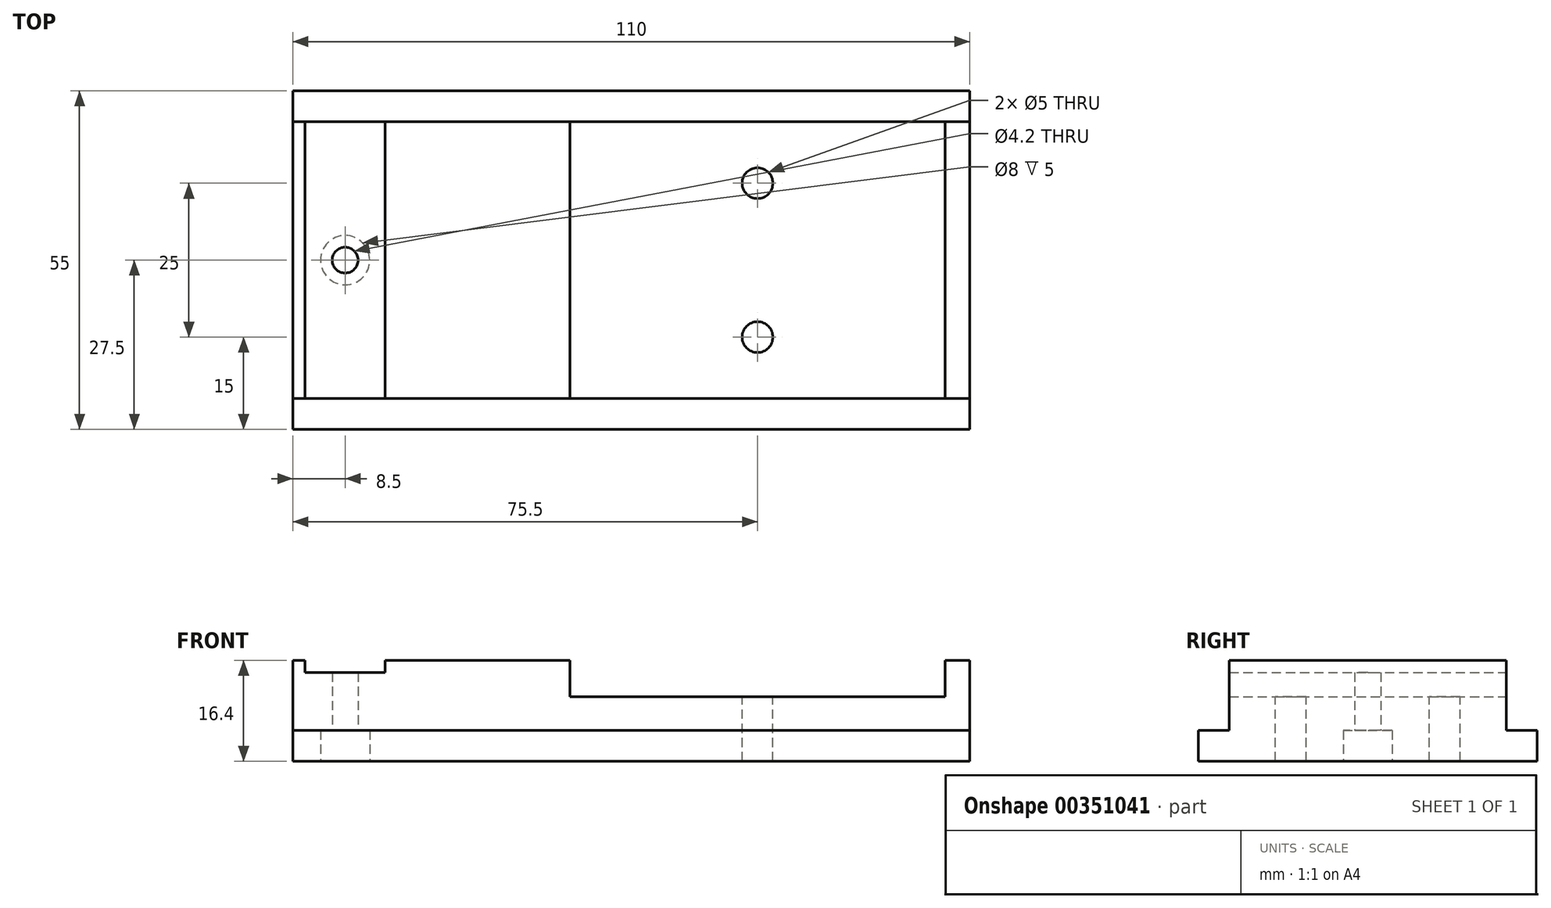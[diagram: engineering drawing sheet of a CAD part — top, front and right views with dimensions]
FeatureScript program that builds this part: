
annotation { "Feature Type Name" : "Feature", "Feature Type Description" : "" }
export const myFeature = defineFeature(function(context is Context, id is Id, definition is map)
    precondition{}
    {
        {
            var Q0;
            Q0=qCreatedBy(makeId("Top.planeOp"),FACE);
            var sketch = newSketch(context, id + "F0", { "sketchPlane" : qUnion([Q0])});
            skLineSegment(sketch, "E0.bottom", {"start": v(55, 27.5) * mm, "end": v(-55, 27.5) * mm});
            skLineSegment(sketch, "E0.top", {"start": v(55, -27.5) * mm, "end": v(-55, -27.5) * mm});
            skLineSegment(sketch, "E0.left", {"start": v(55, 27.5) * mm, "end": v(55, -27.5) * mm});
            skLineSegment(sketch, "E0.right", {"start": v(-55, 27.5) * mm, "end": v(-55, -27.5) * mm});
            skPoint(sketch, "E0.middle", {"position": v(0, 0) * mm});
            skSolve(sketch);
        }
        {
            var Q0;
            Q0 = qSketchRegion(id + "F0", true);
            extrude(context, id + "F1", {"entities" : qUnion([Q0]), "depth" : 5 * mm});
        }
        {
            var Q0;
            Q0=makeQuery(id+"F1.opExtrude","CAP_FACE",FACE,{"disambiguationData":[OSD([sQuery(id+"F0.wireOp",EDGE,"E0.bottom"),sQuery(id+"F0.wireOp",EDGE,"E0.top"),sQuery(id+"F0.wireOp",EDGE,"E0.left"),sQuery(id+"F0.wireOp",EDGE,"E0.right")])],"isStart":false});
            var sketch = newSketch(context, id + "F2", { "sketchPlane" : qUnion([Q0])});
            skLineSegment(sketch, "E1.bottom", {"start": v(55, 22.5) * mm, "end": v(-55, 22.5) * mm});
            skLineSegment(sketch, "E1.top", {"start": v(55, -22.5) * mm, "end": v(-55, -22.5) * mm});
            skLineSegment(sketch, "E1.left", {"start": v(55, 22.5) * mm, "end": v(55, -22.5) * mm});
            skLineSegment(sketch, "E1.right", {"start": v(-55, 22.5) * mm, "end": v(-55, -22.5) * mm});
            skPoint(sketch, "E1.middle", {"position": v(0, 0) * mm});
            skSolve(sketch);
        }
        {
            var Q0;
            Q0=makeQuery(id+"F2.imprint","IMPRINT",FACE,{"disambiguationData":[TD([[makeQuery(id+"F2.imprint","IMPRINT",EDGE,{"derivedFrom":sQuery(id+"F2.wireOp",EDGE,"E1.bottom")}),1.0]])]});
            extrude(context, id + "F3", {"entities" : qUnion([Q0]), "operationType" : NewBodyOperationType.ADD, "depth" : 11.4 * mm});
        }
        {
            var Q0;
            Q0=makeQuery(id+"F3.opExtrude","CAP_FACE",FACE,{"disambiguationData":[OSD([sQuery(id+"F2.wireOp",EDGE,"E1.bottom"),sQuery(id+"F2.wireOp",EDGE,"E1.top"),sQuery(id+"F2.wireOp",EDGE,"E1.left"),sQuery(id+"F2.wireOp",EDGE,"E1.right")])],"isStart":false});
            var sketch = newSketch(context, id + "F4", { "sketchPlane" : qUnion([Q0])});
            skLineSegment(sketch, "E2.bottom", {"start": v(-55, -22.5) * mm, "end": v(-53, -22.5) * mm});
            skLineSegment(sketch, "E2.top", {"start": v(-55, 22.5) * mm, "end": v(-53, 22.5) * mm});
            skLineSegment(sketch, "E2.left", {"start": v(-55, -22.5) * mm, "end": v(-55, 22.5) * mm});
            skLineSegment(sketch, "E2.right", {"start": v(-53, -22.5) * mm, "end": v(-53, 22.5) * mm});
            skLineSegment(sketch, "E3.bottom", {"start": v(-53, -22.5) * mm, "end": v(-40, -22.5) * mm});
            skLineSegment(sketch, "E3.top", {"start": v(-53, 22.5) * mm, "end": v(-40, 22.5) * mm});
            skLineSegment(sketch, "E3.right", {"start": v(-40, -22.5) * mm, "end": v(-40, 22.5) * mm});
            skLineSegment(sketch, "E4.bottom", {"start": v(-40, -22.5) * mm, "end": v(-10, -22.5) * mm});
            skLineSegment(sketch, "E4.top", {"start": v(-40, 22.5) * mm, "end": v(-10, 22.5) * mm});
            skLineSegment(sketch, "E4.right", {"start": v(-10, -22.5) * mm, "end": v(-10, 22.5) * mm});
            skLineSegment(sketch, "E5.bottom", {"start": v(-10, -22.5) * mm, "end": v(51, -22.5) * mm});
            skLineSegment(sketch, "E5.top", {"start": v(-10, 22.5) * mm, "end": v(51, 22.5) * mm});
            skLineSegment(sketch, "E5.right", {"start": v(51, -22.5) * mm, "end": v(51, 22.5) * mm});
            skSolve(sketch);
        }
        {
            var Q0;
            Q0=makeQuery(id+"F4.imprint","IMPRINT",FACE,{"disambiguationData":[TD([[makeQuery(id+"F4.imprint","IMPRINT",EDGE,{"derivedFrom":sQuery(id+"F4.wireOp",EDGE,"E3.bottom")}),-1.0]])]});
            extrude(context, id + "F5", {"entities" : qUnion([Q0]), "operationType" : NewBodyOperationType.REMOVE, "oppositeDirection" : true, "depth" : 2 * mm});
        }
        {
            var Q0;
            Q0=makeQuery(id+"F4.imprint","IMPRINT",FACE,{"disambiguationData":[TD([[makeQuery(id+"F4.imprint","IMPRINT",EDGE,{"derivedFrom":sQuery(id+"F4.wireOp",EDGE,"E5.bottom")}),-1.0]])]});
            extrude(context, id + "F6", {"entities" : qUnion([Q0]), "operationType" : NewBodyOperationType.REMOVE, "oppositeDirection" : true, "depth" : 5.9 * mm});
        }
        {
            var Q0;
            Q0=makeQuery(id+"F1.opExtrude","CAP_FACE",FACE,{"disambiguationData":[OSD([sQuery(id+"F0.wireOp",EDGE,"E0.bottom"),sQuery(id+"F0.wireOp",EDGE,"E0.top"),sQuery(id+"F0.wireOp",EDGE,"E0.left"),sQuery(id+"F0.wireOp",EDGE,"E0.right")])],"isStart":true});
            var sketch = newSketch(context, id + "F7", { "sketchPlane" : qUnion([Q0])});
            skLineSegment(sketch, "E6", {"start": v(-55, 0) * mm, "end": v(-53, 0) * mm});
            skPoint(sketch, "E6.endSnap0", {"position": v(-55, 0) * mm});
            skLineSegment(sketch, "E7", {"start": v(-53, 0) * mm, "end": v(-40, 0) * mm});
            skPoint(sketch, "E8", {"position": v(-46.5, 0) * mm});
            skSolve(sketch);
        }
        {
            var Q0;
            Q0=sQuery(id+"F7.wireOp",VERTEX,"E8");
            var Q1;
            Q1=makeQuery(id+"F1.opExtrude","SWEPT_BODY",BODY,{"disambiguationData":[OSD([sQuery(id+"F0.wireOp",EDGE,"E0.bottom"),sQuery(id+"F0.wireOp",EDGE,"E0.top"),sQuery(id+"F0.wireOp",EDGE,"E0.left"),sQuery(id+"F0.wireOp",EDGE,"E0.right")])]});
            hole(context, id + "F8", {"style" : HoleStyle.C_BORE, "endStyle" : HoleEndStyle.THROUGH, "holeDiameter" : 4.2 * mm, "cBoreDiameter" : 8 * mm, "cBoreDepth" : 5 * mm, "isTappedThrough" : true, "tappedDepth" : 12 * mm, "tapClearance" : 3, "locations" : qUnion([Q0]), "scope" : qUnion([Q1])});
        }
        {
            var Q0;
            Q0=makeQuery(id+"F6.boolean.opBoolean","COPY",FACE,{"derivedFrom":makeQuery(id+"F6.opExtrude","CAP_FACE",FACE,{"disambiguationData":[OSD([sQuery(id+"F4.wireOp",EDGE,"E5.bottom"),sQuery(id+"F4.wireOp",EDGE,"E5.top"),sQuery(id+"F4.wireOp",EDGE,"E4.right"),sQuery(id+"F4.wireOp",EDGE,"E5.right")])],"isStart":false})});
            var sketch = newSketch(context, id + "F9", { "sketchPlane" : qUnion([Q0])});
            skPoint(sketch, "E9", {"position": v(20.5, 22.5) * mm});
            skLineSegment(sketch, "E10", {"start": v(20.5, 22.5) * mm, "end": v(20.5, 12.5) * mm});
            skLineSegment(sketch, "E11", {"start": v(20.5, 12.5) * mm, "end": v(20.5, 0) * mm});
            skLineSegment(sketch, "E12", {"start": v(20.5, 0) * mm, "end": v(20.5, -12.5) * mm});
            skLineSegment(sketch, "E13", {"start": v(20.5, -12.5) * mm, "end": v(20.5, -22.5) * mm});
            skSolve(sketch);
        }
        {
            var Q0;
            Q0=sQuery(id+"F9.wireOp",VERTEX,"E11.start");
            var Q1;
            Q1=sQuery(id+"F9.wireOp",VERTEX,"E13.start");
            var Q2;
            Q2=makeQuery(id+"F1.opExtrude","SWEPT_BODY",BODY,{"disambiguationData":[OSD([sQuery(id+"F0.wireOp",EDGE,"E0.bottom"),sQuery(id+"F0.wireOp",EDGE,"E0.top"),sQuery(id+"F0.wireOp",EDGE,"E0.left"),sQuery(id+"F0.wireOp",EDGE,"E0.right")])]});
            hole(context, id + "F10", {"style" : HoleStyle.SIMPLE, "endStyle" : HoleEndStyle.THROUGH, "standardTappedOrClearance" : lookupTablePath({ "standard" : "Benutzerdefiniert" }), "standardBlindInLast" : lookupTablePath({ "standard" : "Benutzerdefiniert" }), "holeDiameter" : 5 * mm, "isTappedThrough" : true, "tappedDepth" : 12 * mm, "tapClearance" : 3, "locations" : qUnion([Q0, Q1]), "scope" : qUnion([Q2])});
        }
    });
